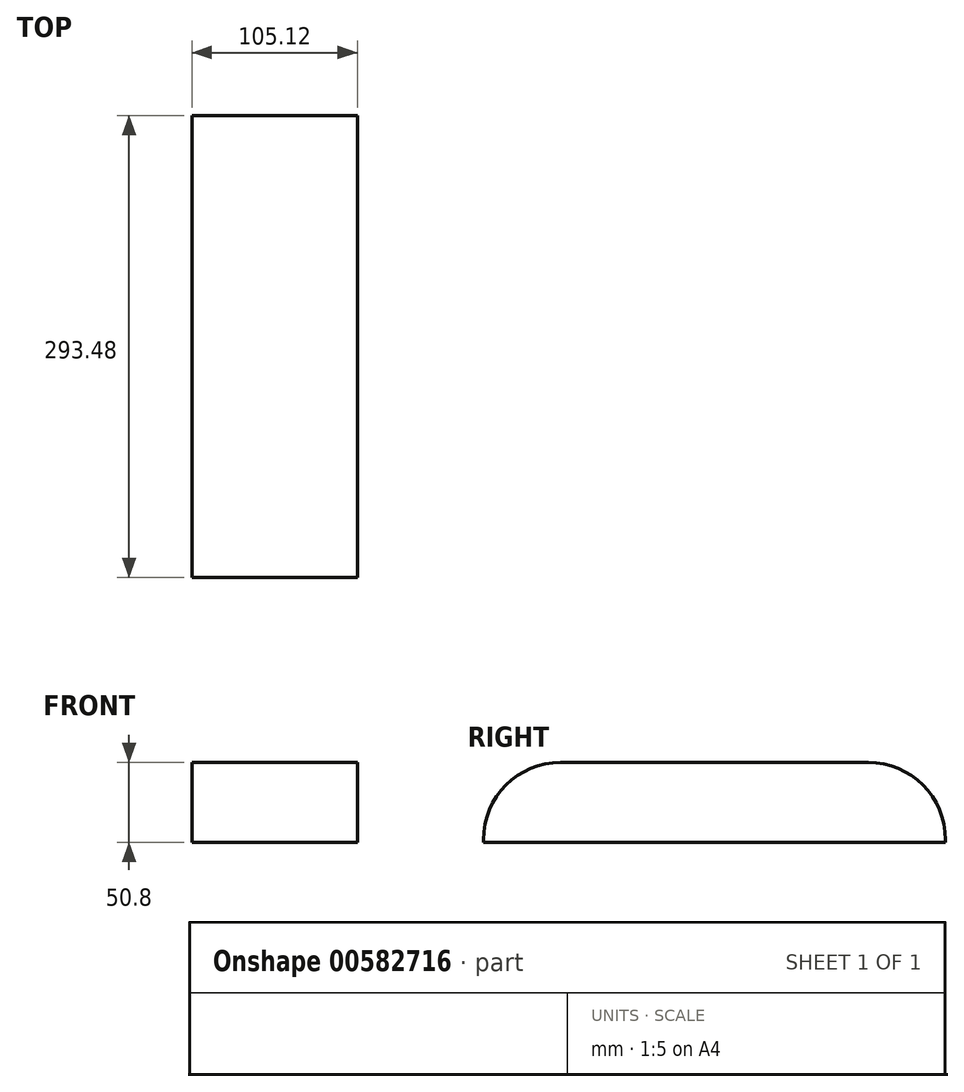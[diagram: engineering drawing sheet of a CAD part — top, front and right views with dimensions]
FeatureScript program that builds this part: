
annotation { "Feature Type Name" : "Feature", "Feature Type Description" : "" }
export const myFeature = defineFeature(function(context is Context, id is Id, definition is map)
    precondition{}
    {
        {
            var Q0;
            Q0=qCreatedBy(makeId("Top.planeOp"),FACE);
            var sketch = newSketch(context, id + "F0", { "sketchPlane" : qUnion([Q0])});
            skLineSegment(sketch, "E0.bottom", {"start": v(-154.98, 53.98) * mm, "end": v(-49.86, 53.98) * mm});
            skLineSegment(sketch, "E0.top", {"start": v(-154.98, -239.5) * mm, "end": v(-49.86, -239.5) * mm});
            skLineSegment(sketch, "E0.left", {"start": v(-154.98, 53.98) * mm, "end": v(-154.98, -239.5) * mm});
            skLineSegment(sketch, "E0.right", {"start": v(-49.86, 53.98) * mm, "end": v(-49.86, -239.5) * mm});
            skLineSegment(sketch, "E1.bottom", {"start": v(-49.86, -239.5) * mm, "end": v(70.02, -239.5) * mm});
            skLineSegment(sketch, "E1.top", {"start": v(-49.86, -202.06) * mm, "end": v(70.02, -202.06) * mm});
            skLineSegment(sketch, "E1.left", {"start": v(-49.86, -239.5) * mm, "end": v(-49.86, -202.06) * mm});
            skLineSegment(sketch, "E1.right", {"start": v(70.02, -239.5) * mm, "end": v(70.02, -202.06) * mm});
            skSolve(sketch);
        }
        {
            var Q0;
            Q0=makeQuery(id+"F0.imprint","IMPRINT",FACE,{"disambiguationData":[TD([[makeQuery(id+"F0.imprint","IMPRINT",EDGE,{"derivedFrom":sQuery(id+"F0.wireOp",EDGE,"E0.bottom")}),-1.0]])]});
            extrude(context, id + "F1", {"entities" : qUnion([Q0]), "depth" : 50.8 * mm, "offsetDistance" : 25.4 * mm});
        }
        {
            var Q0;
            Q0=makeQuery(id+"F1.opExtrude","CAP_EDGE",EDGE,{"disambiguationData":[OSD([sQuery(id+"F0.wireOp",EDGE,"E0.top")])],"isStart":false});
            fillet(context, id + "F2", {"entities" : qUnion([Q0]), "radius" : 49.06 * mm, "tangentPropagation" : true, "allowEdgeOverflow" : false});
        }
        {
            var Q0;
            Q0=makeQuery(id+"F1.opExtrude","CAP_EDGE",EDGE,{"disambiguationData":[OSD([sQuery(id+"F0.wireOp",EDGE,"E0.bottom")])],"isStart":false});
            fillet(context, id + "F3", {"entities" : qUnion([Q0]), "radius" : 49.05 * mm, "tangentPropagation" : true, "allowEdgeOverflow" : false});
        }
    });
